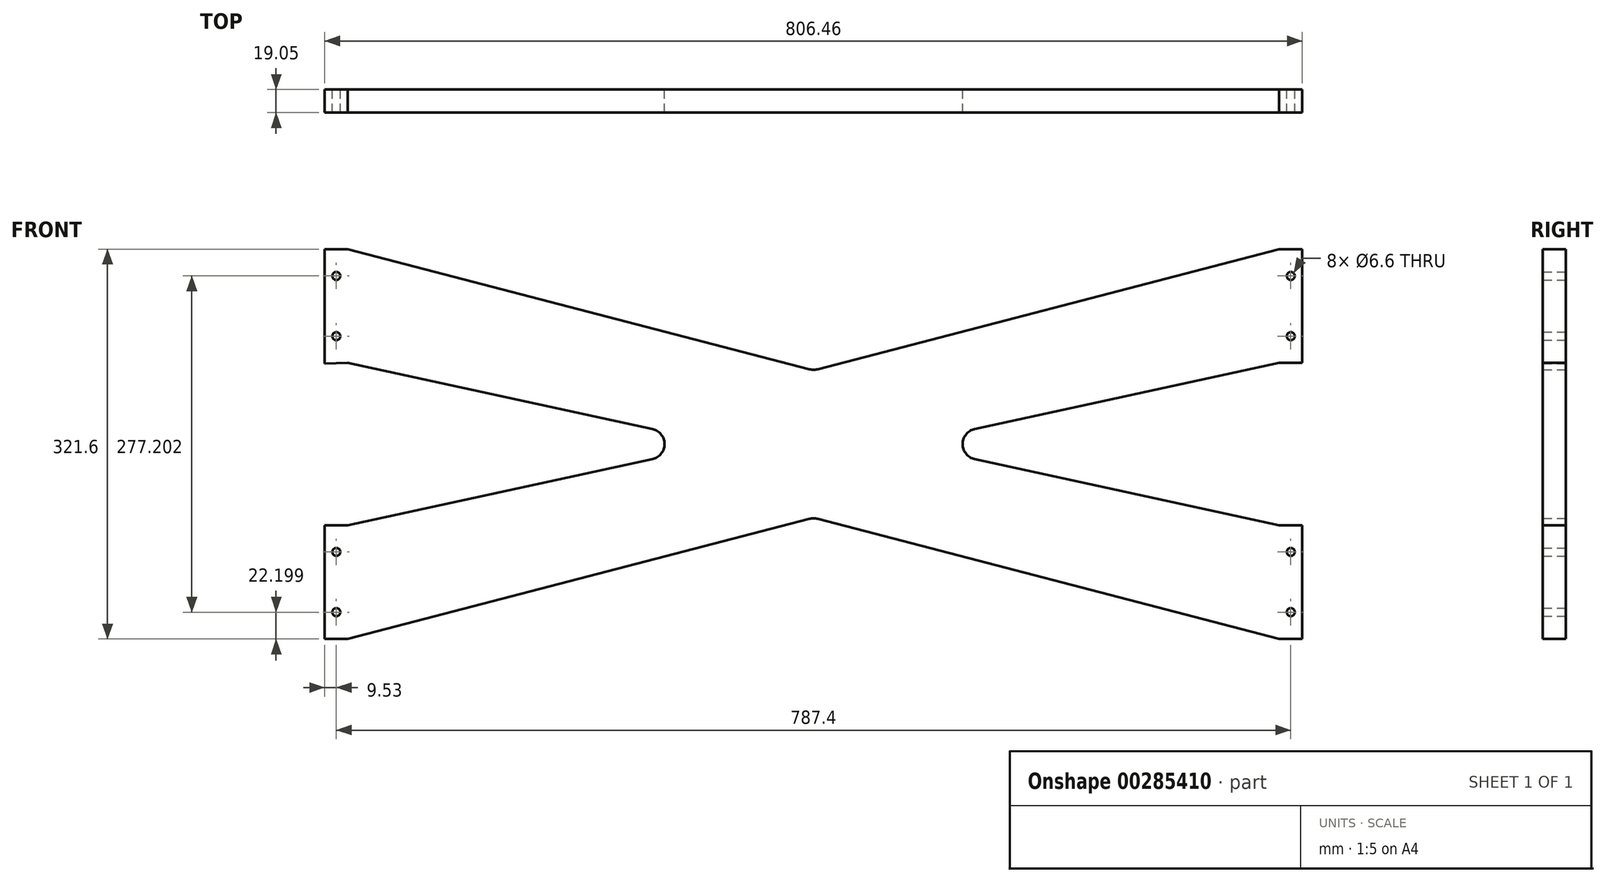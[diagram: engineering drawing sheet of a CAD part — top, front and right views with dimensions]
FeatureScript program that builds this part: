
annotation { "Feature Type Name" : "Feature", "Feature Type Description" : "" }
export const myFeature = defineFeature(function(context is Context, id is Id, definition is map)
    precondition{}
    {
        {
            var Q0;
            Q0=qCreatedBy(makeId("Front.planeOp"),FACE);
            var sketch = newSketch(context, id + "F0", { "sketchPlane" : qUnion([Q0])});
            skLineSegment(sketch, "E0", {"start": v(-384.18, 45.4) * mm, "end": v(428.63, 45.4) * mm, "construction": true});
            skPoint(sketch, "E1.startSnap0", {"position": v(22.22, 45.4) * mm});
            skLineSegment(sketch, "E2", {"start": v(0, 206.2) * mm, "end": v(0, -200.2) * mm, "construction": true});
            skLineSegment(sketch, "E3", {"start": v(-384.18, 112.3) * mm, "end": v(-132.97, 57.81) * mm});
            skLineSegment(sketch, "E4", {"start": v(-384.18, 206.2) * mm, "end": v(-3.2, 107.08) * mm});
            skLineSegment(sketch, "E5.MirrorCS", {"start": v(-384.18, -115.4) * mm, "end": v(-3.2, -16.28) * mm});
            skLineSegment(sketch, "E6.MirrorCS", {"start": v(-384.17, -21.5) * mm, "end": v(-132.97, 32.99) * mm});
            skLineSegment(sketch, "E7.MirrorCS", {"start": v(384.18, 206.2) * mm, "end": v(3.2, 107.08) * mm});
            skLineSegment(sketch, "E8.MirrorCS", {"start": v(384.18, 112.3) * mm, "end": v(132.97, 57.81) * mm});
            skLineSegment(sketch, "E9.MirrorCS", {"start": v(384.18, -21.5) * mm, "end": v(132.97, 32.99) * mm});
            skLineSegment(sketch, "E10.MirrorCS", {"start": v(384.18, -115.4) * mm, "end": v(3.2, -16.28) * mm});
            skPoint(sketch, "E11.visualSharp", {"position": v(0, 106.25) * mm});
            skArc(sketch, "E11.filletArc", {"start": v(-3.2, 107.08) * mm, "mid": v(0, 106.68) * mm, "end": v(3.2, 107.08) * mm});
            skPoint(sketch, "E12.visualSharp", {"position": v(75.74, 45.4) * mm});
            skArc(sketch, "E12.filletArc", {"start": v(132.97, 57.81) * mm, "mid": v(122.96, 45.4) * mm, "end": v(132.97, 32.99) * mm});
            skPoint(sketch, "E13.visualSharp", {"position": v(-75.74, 45.4) * mm});
            skArc(sketch, "E13.filletArc", {"start": v(-132.97, 32.99) * mm, "mid": v(-122.96, 45.4) * mm, "end": v(-132.97, 57.81) * mm});
            skPoint(sketch, "E14.visualSharp", {"position": v(0, -15.45) * mm});
            skArc(sketch, "E14.filletArc", {"start": v(3.2, -16.28) * mm, "mid": v(0, -15.88) * mm, "end": v(-3.2, -16.28) * mm});
            skLineSegment(sketch, "E15", {"start": v(-384.18, 206.2) * mm, "end": v(-403.23, 206.2) * mm});
            skLineSegment(sketch, "E16", {"start": v(-403.23, 206.2) * mm, "end": v(-403.23, 111.6) * mm});
            skLineSegment(sketch, "E17", {"start": v(-403.23, 111.6) * mm, "end": v(-384.18, 112.3) * mm});
            skLineSegment(sketch, "E18", {"start": v(-384.18, -21.5) * mm, "end": v(-403.22, -21.5) * mm});
            skLineSegment(sketch, "E19", {"start": v(-403.22, -21.5) * mm, "end": v(-403.22, -115.32) * mm});
            skLineSegment(sketch, "E20", {"start": v(-403.22, -115.32) * mm, "end": v(-384.18, -115.4) * mm});
            skLineSegment(sketch, "E21", {"start": v(384.18, 206.2) * mm, "end": v(403.23, 206.2) * mm});
            skLineSegment(sketch, "E22", {"start": v(403.23, 206.2) * mm, "end": v(403.23, 112.3) * mm});
            skLineSegment(sketch, "E23", {"start": v(403.23, 112.3) * mm, "end": v(384.18, 112.3) * mm});
            skLineSegment(sketch, "E24", {"start": v(384.18, -115.4) * mm, "end": v(403.23, -115.4) * mm});
            skLineSegment(sketch, "E25", {"start": v(403.23, -115.4) * mm, "end": v(403.23, -21.5) * mm});
            skLineSegment(sketch, "E26", {"start": v(403.23, -21.5) * mm, "end": v(384.18, -21.5) * mm});
            skSolve(sketch);
        }
        {
            var Q0;
            Q0 = qSketchRegion(id + "F0", true);
            extrude(context, id + "F1", {"entities" : qUnion([Q0]), "depth" : 19.05 * mm});
        }
        {
            var Q0;
            Q0=makeQuery(id+"F0.imprint","IMPRINT",FACE,{"disambiguationData":[TD([[makeQuery(id+"F0.imprint","IMPRINT",EDGE,{"derivedFrom":sQuery(id+"F0.wireOp",EDGE,"E3")}),1.0]])]});
            var sketch = newSketch(context, id + "F2", { "sketchPlane" : qUnion([Q0])});
            skLineSegment(sketch, "E27.0", {"start": v(403.23, 112.3) * mm, "end": v(384.18, 112.3) * mm});
            skLineSegment(sketch, "E28", {"start": v(393.7, 112.3) * mm, "end": v(393.7, 206.1) * mm, "construction": true});
            skCircle(sketch, "E29", {"center": v(393.7, 184) * mm, "radius": 3.3 * mm});
            skCircle(sketch, "E30", {"center": v(393.7, 134.36) * mm, "radius": 3.3 * mm});
            skLineSegment(sketch, "E31.0", {"start": v(0, 206.2) * mm, "end": v(0, -200.2) * mm, "construction": true});
            skLineSegment(sketch, "E32.0", {"start": v(-384.18, 45.4) * mm, "end": v(428.63, 45.4) * mm, "construction": true});
            skCircle(sketch, "E33.MirrorC", {"center": v(-393.7, 184) * mm, "radius": 3.3 * mm});
            skCircle(sketch, "E34.MirrorC", {"center": v(-393.7, 134.36) * mm, "radius": 3.3 * mm});
            skCircle(sketch, "E35.MirrorC", {"center": v(393.7, -43.56) * mm, "radius": 3.3 * mm});
            skCircle(sketch, "E36.MirrorC", {"center": v(393.7, -93.2) * mm, "radius": 3.3 * mm});
            skCircle(sketch, "E37.MirrorC", {"center": v(-393.7, -93.2) * mm, "radius": 3.3 * mm});
            skCircle(sketch, "E38.MirrorC", {"center": v(-393.7, -43.56) * mm, "radius": 3.3 * mm});
            skSolve(sketch);
        }
        {
            var Q0;
            Q0 = qSketchRegion(id + "F2", true);
            var Q1;
            Q1=makeQuery(id+"F1.opExtrude","CAP_FACE",FACE,{"disambiguationData":[OSD([sQuery(id+"F0.wireOp",EDGE,"E3"),sQuery(id+"F0.wireOp",EDGE,"E4"),sQuery(id+"F0.wireOp",EDGE,"E5.MirrorCS"),sQuery(id+"F0.wireOp",EDGE,"E6.MirrorCS"),sQuery(id+"F0.wireOp",EDGE,"E7.MirrorCS"),sQuery(id+"F0.wireOp",EDGE,"E8.MirrorCS"),sQuery(id+"F0.wireOp",EDGE,"E9.MirrorCS"),sQuery(id+"F0.wireOp",EDGE,"E10.MirrorCS"),sQuery(id+"F0.wireOp",EDGE,"E11.filletArc"),sQuery(id+"F0.wireOp",EDGE,"E12.filletArc"),sQuery(id+"F0.wireOp",EDGE,"E13.filletArc"),sQuery(id+"F0.wireOp",EDGE,"E14.filletArc"),sQuery(id+"F0.wireOp",EDGE,"E15"),sQuery(id+"F0.wireOp",EDGE,"E16"),sQuery(id+"F0.wireOp",EDGE,"E17"),sQuery(id+"F0.wireOp",EDGE,"E18"),sQuery(id+"F0.wireOp",EDGE,"E19"),sQuery(id+"F0.wireOp",EDGE,"E20"),sQuery(id+"F0.wireOp",EDGE,"E21"),sQuery(id+"F0.wireOp",EDGE,"E22"),sQuery(id+"F0.wireOp",EDGE,"E23"),sQuery(id+"F0.wireOp",EDGE,"E24"),sQuery(id+"F0.wireOp",EDGE,"E25"),sQuery(id+"F0.wireOp",EDGE,"E26")])],"isStart":false});
            extrude(context, id + "F3", {"entities" : qUnion([Q0]), "operationType" : NewBodyOperationType.REMOVE, "endBound" : BoundingType.UP_TO_SURFACE, "endBoundEntityFace" : qUnion([Q1]), "depth" : 25.4 * mm});
        }
    });
